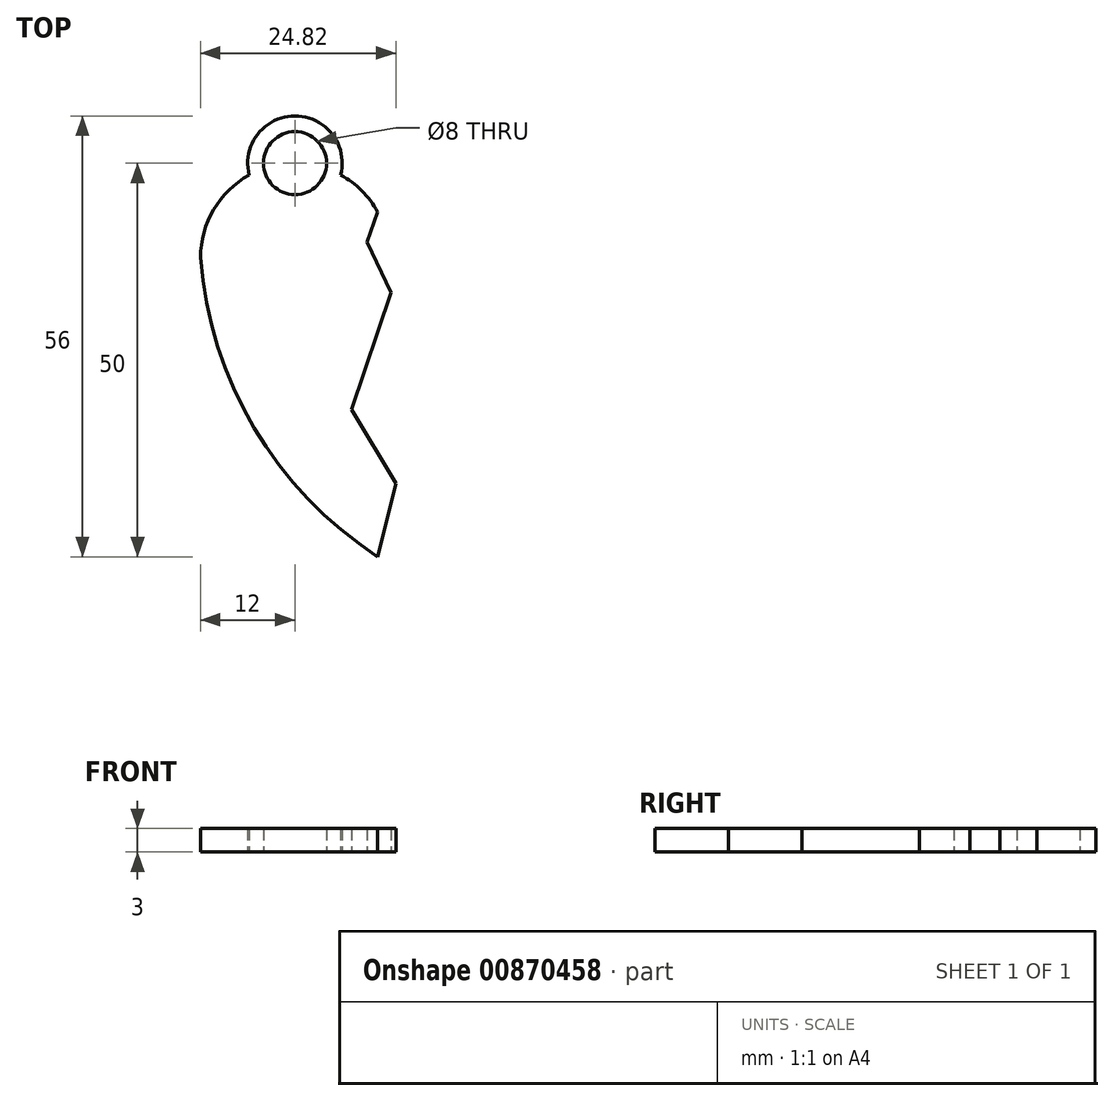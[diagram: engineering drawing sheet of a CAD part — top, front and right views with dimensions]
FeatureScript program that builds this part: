
annotation { "Feature Type Name" : "Feature", "Feature Type Description" : "" }
export const myFeature = defineFeature(function(context is Context, id is Id, definition is map)
    precondition{}
    {
        {
            var Q0;
            Q0=qCreatedBy(makeId("Top.planeOp"),FACE);
            var sketch = newSketch(context, id + "F0", { "sketchPlane" : qUnion([Q0])});
            skLineSegment(sketch, "E0", {"start": v(0, 0) * mm, "end": v(0, -20) * mm, "construction": true});
            skLineSegment(sketch, "E1", {"start": v(0, 4) * mm, "end": v(0, 0) * mm, "construction": true});
            skLineSegment(sketch, "E2", {"start": v(0, 0) * mm, "end": v(0, -10) * mm, "construction": true});
            skLineSegment(sketch, "E3", {"start": v(0, 0) * mm, "end": v(0, -2) * mm, "construction": true});
            skLineSegment(sketch, "E4", {"start": v(0, -2) * mm, "end": v(-10.5, -2) * mm, "construction": true});
            skLineSegment(sketch, "E5", {"start": v(0, -2) * mm, "end": v(10.5, -2) * mm, "construction": true});
            skPoint(sketch, "E6.centerSnap0", {"position": v(-5.25, -2) * mm});
            skLineSegment(sketch, "E7", {"start": v(0, 0) * mm, "end": v(0, -40) * mm, "construction": true});
            skCircle(sketch, "E8", {"center": v(-10.5, -2) * mm, "radius": 12 * mm});
            skCircle(sketch, "E9", {"center": v(10.5, -2) * mm, "radius": 12 * mm});
            skArc(sketch, "E10", {"start": v(-22.5, -2) * mm, "mid": v(-15.67, -23.62) * mm, "end": v(0, -40) * mm});
            skArc(sketch, "E11", {"start": v(0, -40) * mm, "mid": v(15.67, -23.62) * mm, "end": v(22.5, -2) * mm});
            skLineSegment(sketch, "E12", {"start": v(0, 3.8) * mm, "end": v(-1.33, 0) * mm});
            skLineSegment(sketch, "E13", {"start": v(-1.33, 0) * mm, "end": v(1.72, -6.43) * mm});
            skLineSegment(sketch, "E14", {"start": v(1.72, -6.43) * mm, "end": v(-3.32, -21.32) * mm});
            skLineSegment(sketch, "E15", {"start": v(-3.32, -21.32) * mm, "end": v(2.32, -30.68) * mm});
            skLineSegment(sketch, "E16", {"start": v(2.32, -30.68) * mm, "end": v(0, -40) * mm});
            skLineSegment(sketch, "E17", {"start": v(-10.5, -2) * mm, "end": v(-10.5, 10) * mm, "construction": true});
            skCircle(sketch, "E18", {"center": v(-10.5, 10) * mm, "radius": 6 * mm});
            skCircle(sketch, "E19", {"center": v(-10.5, 10) * mm, "radius": 4 * mm});
            skLineSegment(sketch, "E20", {"start": v(10.5, -2) * mm, "end": v(10.5, 10) * mm, "construction": true});
            skCircle(sketch, "E21", {"center": v(10.5, 10) * mm, "radius": 6 * mm});
            skCircle(sketch, "E22", {"center": v(10.5, 10) * mm, "radius": 4 * mm});
            skSolve(sketch);
        }
        {
            var Q0;
            {var subQ0=sQuery(id+"F0.wireOp",EDGE,"E18");var subQ1=sQuery(id+"F0.wireOp",EDGE,"E8");var subQ2=makeQuery(id+"F0.imprint","INTERSECT",VERTEX,{"disambiguationData":[OD(0.0)],"derivedFrom":[subQ1,subQ0]});Q0=makeQuery(id+"F0.imprint","IMPRINT",FACE,{"disambiguationData":[TD([[makeQuery(id+"F0.imprint","IMPRINT",EDGE,{"disambiguationData":[TD([[subQ2,-1.0]])],"derivedFrom":subQ1}),-1.0]])]});}
            var Q1;
            {var subQ0=sQuery(id+"F0.wireOp",EDGE,"E18");var subQ1=sQuery(id+"F0.wireOp",EDGE,"E8");var subQ2=makeQuery(id+"F0.imprint","INTERSECT",VERTEX,{"disambiguationData":[OD(0.0)],"derivedFrom":[subQ1,subQ0]});Q1=makeQuery(id+"F0.imprint","IMPRINT",FACE,{"disambiguationData":[TD([[makeQuery(id+"F0.imprint","IMPRINT",EDGE,{"disambiguationData":[TD([[subQ2,-1.0]])],"derivedFrom":subQ1}),1.0]])]});}
            var Q2;
            {var subQ0=sQuery(id+"F0.wireOp",EDGE,"E10");var subQ1=sQuery(id+"F0.wireOp",EDGE,"E8");var subQ8=makeQuery(id+"F0.imprint","INTERSECT",VERTEX,{"disambiguationData":[OD(0.0)],"derivedFrom":[subQ1,subQ0]});Q2=makeQuery(id+"F0.imprint","IMPRINT",FACE,{"disambiguationData":[TD([[makeQuery(id+"F0.imprint","IMPRINT",EDGE,{"disambiguationData":[TD([[subQ8,1.0]])],"derivedFrom":subQ1}),1.0]])]});}
            var Q3;
            {var subQ0=sQuery(id+"F0.wireOp",EDGE,"E9");var subQ1=sQuery(id+"F0.wireOp",EDGE,"E8");var subQ2=makeQuery(id+"F0.imprint","INTERSECT",VERTEX,{"derivedFrom":[subQ1,subQ0]});Q3=makeQuery(id+"F0.imprint","IMPRINT",FACE,{"disambiguationData":[TD([[makeQuery(id+"F0.imprint","IMPRINT",EDGE,{"disambiguationData":[TD([[subQ2,-1.0]])],"derivedFrom":subQ1}),1.0]])]});}
            var Q4;
            {var subQ0=sQuery(id+"F0.wireOp",EDGE,"E9");var subQ1=sQuery(id+"F0.wireOp",EDGE,"E8");var subQ2=makeQuery(id+"F0.imprint","INTERSECT",VERTEX,{"derivedFrom":[subQ1,subQ0]});Q4=makeQuery(id+"F0.imprint","IMPRINT",FACE,{"disambiguationData":[TD([[makeQuery(id+"F0.imprint","IMPRINT",EDGE,{"disambiguationData":[TD([[subQ2,-1.0]])],"derivedFrom":subQ1}),-1.0]])]});}
            var Q5;
            {var subQ0=sQuery(id+"F0.wireOp",EDGE,"E15");Q5=makeQuery(id+"F0.imprint","IMPRINT",FACE,{"disambiguationData":[TD([[makeQuery(id+"F0.imprint","IMPRINT",EDGE,{"derivedFrom":subQ0}),-1.0]])]});}
            var Q6;
            {var subQ0=sQuery(id+"F0.wireOp",EDGE,"E12");Q6=makeQuery(id+"F0.imprint","IMPRINT",FACE,{"disambiguationData":[TD([[makeQuery(id+"F0.imprint","IMPRINT",EDGE,{"derivedFrom":subQ0}),-1.0]])]});}
            extrude(context, id + "F1", {"entities" : qUnion([Q0, Q1, Q2, Q3, Q4, Q5, Q6]), "depth" : 3 * mm, "offsetDistance" : 25 * mm});
        }
    });
